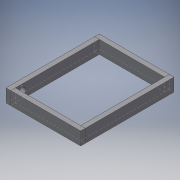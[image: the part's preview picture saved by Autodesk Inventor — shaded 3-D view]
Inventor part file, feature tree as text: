
AUTODESK INVENTOR PART (.ipt)
format: ipt  version: 2016 (Build 200138000, 138)  size: 166,400 bytes
history: native  units: in
note: dims shown in document units (in); Inventor stores cm internally (conversion verified against a paired STEP export)
features: sketch x7, split x4, extrude x2, boolean_combine x2, hole x1
ambient origin geometry x8: Origin, YZ Plane, XZ Plane, XY Plane, X Axis, Y Axis, Z Axis, Center Point
bodies: Solid1 (feature_tree), Solid2 (feature_tree), Solid3 (feature_tree), Solid4 (feature_tree), Solid5 (feature_tree), Solid6 (feature_tree), Solid7 (feature_tree), Solid8 (feature_tree), Solid9 (feature_tree)
feature tree (16):
  extrude  "Extrusion1"  Depth=16.0in
  extrude  "Extrusion2"  Depth=18.0in
  split  "Split1"
  split  "Split2"
  split  "Split3"
  split  "Split4"
  boolean_combine  "Combine1"
  boolean_combine  "Combine2"
  hole  "Hole1"  [1 undecoded]
  sketch  "Sketch1"  dims[d0=20.0in d1=16.0in]
  sketch  "Sketch2"  dims[d2=2.8in d3=0.0in d4=18.0in]
  sketch  "Sketch3"  dims[d5=14.0in d7=2.8in d8=0.0in]
  sketch  "Sketch4"  dims[d9=1.5in]
  sketch  "Sketch5"  dims[d10=2.5in]
  sketch  "Sketch6"  dims[d11=1.5in d12=0.75in d13=0.375in d14=0.25in d15=0.5635in d16=1.0in d17=0.8108in]
  sketch  "Sketch7"
note: 1 required parameter value undecoded (feature->parameter linkage not recoverable at this tier; creation-order binding heuristic only, values carry confidence <= 0.55)
